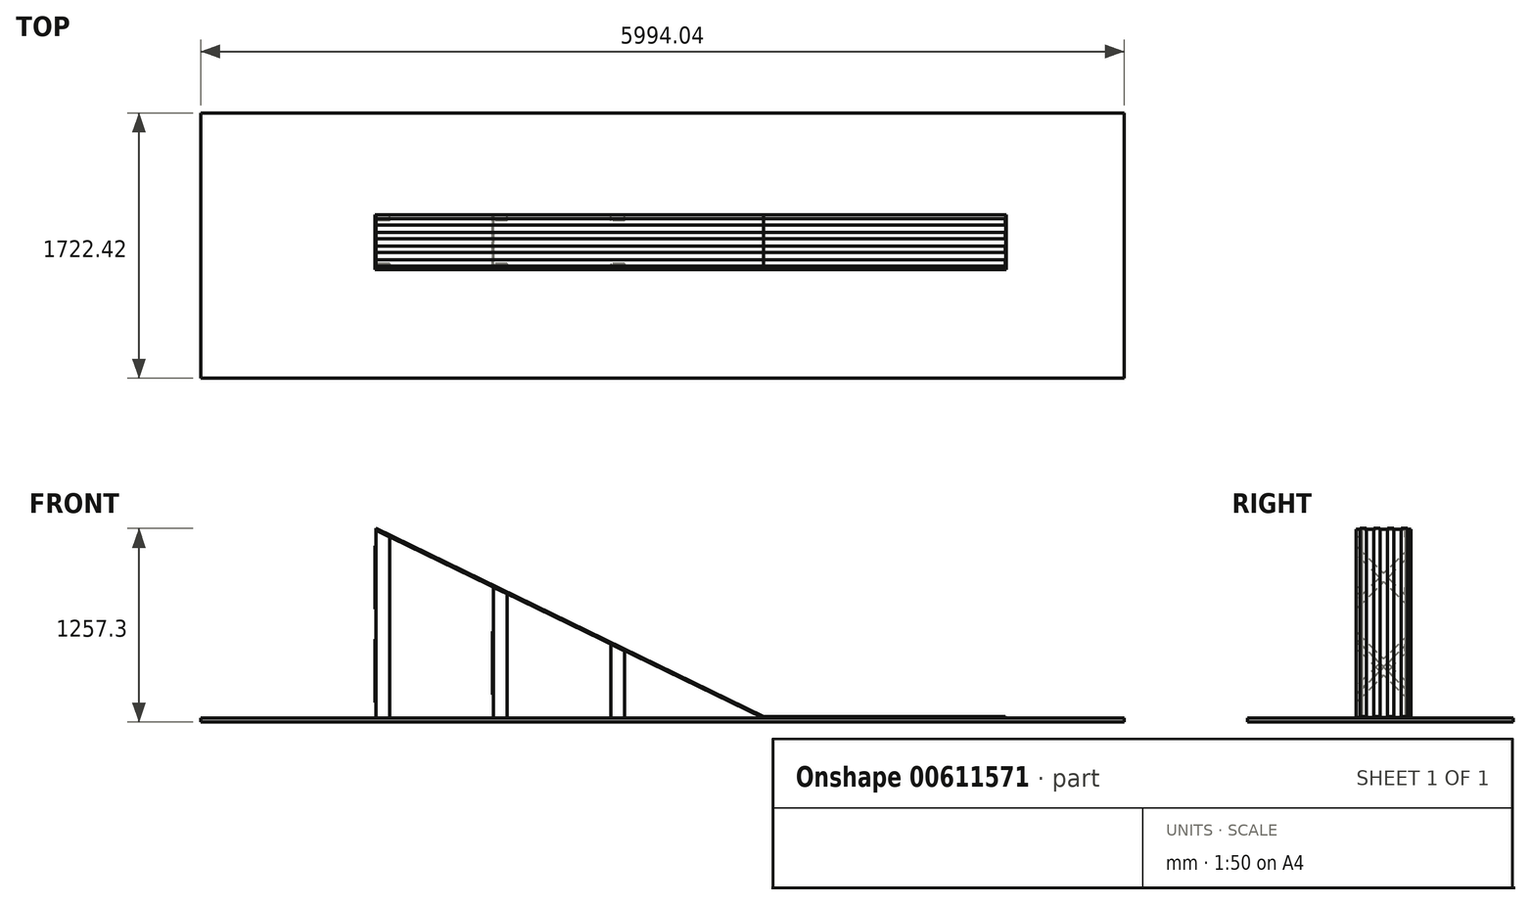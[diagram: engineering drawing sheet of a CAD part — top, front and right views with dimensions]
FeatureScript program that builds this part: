
annotation { "Feature Type Name" : "Feature", "Feature Type Description" : "" }
export const myFeature = defineFeature(function(context is Context, id is Id, definition is map)
    precondition{}
    {
        {
            var Q0;
            Q0=qCreatedBy(makeId("Front.planeOp"),FACE);
            var sketch = newSketch(context, id + "F0", { "sketchPlane" : qUnion([Q0])});
            skLineSegment(sketch, "E0", {"start": v(0, 0) * mm, "end": v(2514.6, -1219.2) * mm});
            skLineSegment(sketch, "E1", {"start": v(2514.6, -1219.2) * mm, "end": v(4089.4, -1219.2) * mm});
            skSolve(sketch);
        }
        {
            var Q0;
            Q0=qCreatedBy(makeId("Right.planeOp"),FACE);
            var sketch = newSketch(context, id + "F1", { "sketchPlane" : qUnion([Q0])});
            skLineSegment(sketch, "E2.bottom", {"start": v(177.8, 0) * mm, "end": v(-177.8, 0) * mm});
            skLineSegment(sketch, "E2.top", {"start": v(177.8, 6.35) * mm, "end": v(153.99, 6.35) * mm});
            skLineSegment(sketch, "E2.left", {"start": v(177.8, 0) * mm, "end": v(177.8, 6.35) * mm});
            skLineSegment(sketch, "E2.right", {"start": v(-177.8, 0) * mm, "end": v(-177.8, 6.35) * mm});
            skLineSegment(sketch, "E3.bottom", {"start": v(-153.99, 12.7) * mm, "end": v(-112.71, 12.7) * mm});
            skLineSegment(sketch, "E3.left", {"start": v(-153.99, 12.7) * mm, "end": v(-153.99, 6.35) * mm});
            skLineSegment(sketch, "E3.right", {"start": v(-112.71, 12.7) * mm, "end": v(-112.71, 6.35) * mm});
            skLineSegment(sketch, "E4.trimOffspring", {"start": v(-153.99, 6.35) * mm, "end": v(-177.8, 6.35) * mm});
            skLineSegment(sketch, "E5.bottom", {"start": v(-65.09, 12.7) * mm, "end": v(-23.81, 12.7) * mm});
            skLineSegment(sketch, "E5.left", {"start": v(-65.09, 12.7) * mm, "end": v(-65.09, 6.35) * mm});
            skLineSegment(sketch, "E5.right", {"start": v(-23.81, 12.7) * mm, "end": v(-23.81, 6.35) * mm});
            skLineSegment(sketch, "E6.trimOffspring", {"start": v(-65.09, 6.35) * mm, "end": v(-112.71, 6.35) * mm});
            skLineSegment(sketch, "E7.MirrorCS", {"start": v(153.99, 12.7) * mm, "end": v(153.99, 6.35) * mm});
            skLineSegment(sketch, "E8.MirrorCS", {"start": v(153.99, 12.7) * mm, "end": v(112.71, 12.7) * mm});
            skLineSegment(sketch, "E9.MirrorCS", {"start": v(65.09, 6.35) * mm, "end": v(112.71, 6.35) * mm});
            skLineSegment(sketch, "E10.MirrorCS", {"start": v(112.71, 12.7) * mm, "end": v(112.71, 6.35) * mm});
            skLineSegment(sketch, "E11.MirrorCS", {"start": v(153.99, 6.35) * mm, "end": v(177.8, 6.35) * mm});
            skLineSegment(sketch, "E12.MirrorCS", {"start": v(23.81, 12.7) * mm, "end": v(23.81, 6.35) * mm});
            skLineSegment(sketch, "E13.MirrorCS", {"start": v(65.09, 12.7) * mm, "end": v(23.81, 12.7) * mm});
            skLineSegment(sketch, "E14.MirrorCS", {"start": v(65.09, 12.7) * mm, "end": v(65.09, 6.35) * mm});
            skLineSegment(sketch, "E15.trimOffspring", {"start": v(23.81, 6.35) * mm, "end": v(-23.81, 6.35) * mm});
            skLineSegment(sketch, "E16.trimOffspring", {"start": v(112.71, 6.35) * mm, "end": v(65.09, 6.35) * mm});
            skSolve(sketch);
        }
        {
            var Q0;
            Q0=makeQuery(id+"F1.imprint","IMPRINT",FACE,{"disambiguationData":[TD([[makeQuery(id+"F1.imprint","IMPRINT",EDGE,{"derivedFrom":sQuery(id+"F1.wireOp",EDGE,"E2.bottom")}),-1.0]])]});
            var Q1;
            Q1=qConstructionFilter(qBodyType(qCreatedBy(id+"F0",EDGE),BodyType.WIRE),ConstructionObject.NO);
            sweep(context, id + "F2", {"profiles" : qUnion([Q0]), "path" : qUnion([Q1])});
        }
        {
            var Q0;
            Q0=qCreatedBy(makeId("Top.planeOp"),FACE);
            cPlane(context, id + "F3", {"entities" : qUnion([Q0]), "cplaneType" : CPlaneType.OFFSET, "offset" : 1219.2 * mm, "oppositeDirection" : true, "width" : 152.4 * mm, "height" : 152.4 * mm});
        }
        {
            var Q0;
            Q0=qCreatedBy(id+"F3.planeOp",FACE);
            var sketch = newSketch(context, id + "F4", { "sketchPlane" : qUnion([Q0])});
            skLineSegment(sketch, "E17.bottom", {"start": v(-1136.8, 840.01) * mm, "end": v(4857.24, 840.01) * mm});
            skLineSegment(sketch, "E17.top", {"start": v(-1136.8, -882.41) * mm, "end": v(4857.24, -882.41) * mm});
            skLineSegment(sketch, "E17.left", {"start": v(-1136.8, 840.01) * mm, "end": v(-1136.8, -882.41) * mm});
            skLineSegment(sketch, "E17.right", {"start": v(4857.24, 840.01) * mm, "end": v(4857.24, -882.41) * mm});
            skSolve(sketch);
        }
        {
            var Q0;
            Q0=makeQuery(id+"F4.imprint","IMPRINT",FACE,{"disambiguationData":[TD([[makeQuery(id+"F4.imprint","IMPRINT",EDGE,{"derivedFrom":sQuery(id+"F4.wireOp",EDGE,"E17.bottom")}),-1.0]])]});
            var Q1;
            Q1=sQuery(id+"F4.wireOp",EDGE,"E17.top");
            extrude(context, id + "F5", {"entities" : qUnion([Q0]), "surfaceEntities" : qUnion([Q1]), "oppositeDirection" : true, "depth" : 25.4 * mm, "offsetDistance" : 25.4 * mm});
        }
        {
            var Q0;
            Q0=qCreatedBy(id+"F3.planeOp",FACE);
            var sketch = newSketch(context, id + "F6", { "sketchPlane" : qUnion([Q0])});
            skLineSegment(sketch, "E18.bottom", {"start": v(0, 177.8) * mm, "end": v(88.9, 177.8) * mm});
            skLineSegment(sketch, "E18.top", {"start": v(0, 139.7) * mm, "end": v(88.9, 139.7) * mm});
            skLineSegment(sketch, "E18.left", {"start": v(0, 177.8) * mm, "end": v(0, 139.7) * mm});
            skLineSegment(sketch, "E18.right", {"start": v(88.9, 177.8) * mm, "end": v(88.9, 139.7) * mm});
            skLineSegment(sketch, "E19.bottom", {"start": v(762, 177.8) * mm, "end": v(850.9, 177.8) * mm});
            skLineSegment(sketch, "E19.top", {"start": v(762, 139.7) * mm, "end": v(850.9, 139.7) * mm});
            skLineSegment(sketch, "E19.left", {"start": v(762, 177.8) * mm, "end": v(762, 139.7) * mm});
            skLineSegment(sketch, "E19.right", {"start": v(850.9, 177.8) * mm, "end": v(850.9, 139.7) * mm});
            skLineSegment(sketch, "E20.bottom", {"start": v(1524, 177.8) * mm, "end": v(1612.9, 177.8) * mm});
            skLineSegment(sketch, "E20.top", {"start": v(1524, 139.7) * mm, "end": v(1612.9, 139.7) * mm});
            skLineSegment(sketch, "E20.left", {"start": v(1524, 177.8) * mm, "end": v(1524, 139.7) * mm});
            skLineSegment(sketch, "E20.right", {"start": v(1612.9, 177.8) * mm, "end": v(1612.9, 139.7) * mm});
            skLineSegment(sketch, "E21.MirrorCS", {"start": v(88.9, -177.8) * mm, "end": v(88.9, -139.7) * mm});
            skLineSegment(sketch, "E22.MirrorCS", {"start": v(0, -139.7) * mm, "end": v(88.9, -139.7) * mm});
            skLineSegment(sketch, "E23.MirrorCS", {"start": v(0, -177.8) * mm, "end": v(0, -139.7) * mm});
            skLineSegment(sketch, "E24.MirrorCS", {"start": v(762, -177.8) * mm, "end": v(850.9, -177.8) * mm});
            skLineSegment(sketch, "E25.MirrorCS", {"start": v(762, -139.7) * mm, "end": v(850.9, -139.7) * mm});
            skLineSegment(sketch, "E26.MirrorCS", {"start": v(0, -177.8) * mm, "end": v(88.9, -177.8) * mm});
            skLineSegment(sketch, "E27.MirrorCS", {"start": v(1612.9, -177.8) * mm, "end": v(1612.9, -139.7) * mm});
            skLineSegment(sketch, "E28.MirrorCS", {"start": v(1524, -177.8) * mm, "end": v(1524, -139.7) * mm});
            skLineSegment(sketch, "E29.MirrorCS", {"start": v(1524, -139.7) * mm, "end": v(1612.9, -139.7) * mm});
            skLineSegment(sketch, "E30.MirrorCS", {"start": v(762, -177.8) * mm, "end": v(762, -139.7) * mm});
            skLineSegment(sketch, "E31.MirrorCS", {"start": v(1524, -177.8) * mm, "end": v(1612.9, -177.8) * mm});
            skLineSegment(sketch, "E32.MirrorCS", {"start": v(850.9, -177.8) * mm, "end": v(850.9, -139.7) * mm});
            skSolve(sketch);
        }
        {
            var Q0;
            Q0=qSketchRegion(id+"F6",true);
            var Q1;
            Q1=makeQuery(id+"F2.opSweep","SWEPT_FACE",FACE,{"disambiguationData":[OSD([sQuery(id+"F0.wireOp",EDGE,"E0"),sQuery(id+"F1.wireOp",EDGE,"E2.bottom")])]});
            extrude(context, id + "F7", {"entities" : qUnion([Q0]), "endBound" : BoundingType.UP_TO_SURFACE, "depth" : 25.4 * mm, "endBoundEntityFace" : qUnion([Q1]), "offsetDistance" : 25.4 * mm});
        }
        {
            var Q0;
            Q0=qCreatedBy(makeId("Right.planeOp"),FACE);
            var sketch = newSketch(context, id + "F8", { "sketchPlane" : qUnion([Q0])});
            skLineSegment(sketch, "E33", {"start": v(177.8, -101.6) * mm, "end": v(0, -279.4) * mm});
            skLineSegment(sketch, "E34", {"start": v(-177.8, -511.08) * mm, "end": v(-177.8, -457.2) * mm});
            skLineSegment(sketch, "E35", {"start": v(-177.8, -511.08) * mm, "end": v(0, -333.28) * mm});
            skLineSegment(sketch, "E36", {"start": v(177.8, -101.6) * mm, "end": v(177.8, -155.48) * mm});
            skLineSegment(sketch, "E37", {"start": v(-177.8, -511.08) * mm, "end": v(-204.74, -484.14) * mm, "construction": true});
            skLineSegment(sketch, "E38", {"start": v(-204.74, -484.14) * mm, "end": v(-177.8, -457.2) * mm, "construction": true});
            skLineSegment(sketch, "E39", {"start": v(177.8, -155.48) * mm, "end": v(204.74, -128.54) * mm, "construction": true});
            skLineSegment(sketch, "E40", {"start": v(204.74, -128.54) * mm, "end": v(177.8, -101.6) * mm, "construction": true});
            skLineSegment(sketch, "E41", {"start": v(130.23, -609.6) * mm, "end": v(-102.74, -609.6) * mm, "construction": true});
            skLineSegment(sketch, "E42.MirrorCS", {"start": v(177.8, -511.08) * mm, "end": v(177.8, -457.2) * mm});
            skLineSegment(sketch, "E43.MirrorCS", {"start": v(-177.8, -101.6) * mm, "end": v(-177.8, -155.48) * mm});
            skLineSegment(sketch, "E44.MirrorCS", {"start": v(177.8, -511.08) * mm, "end": v(0, -333.28) * mm});
            skLineSegment(sketch, "E45.MirrorCS", {"start": v(-177.8, -101.6) * mm, "end": v(0, -279.4) * mm});
            skLineSegment(sketch, "E46.trimOffspring", {"start": v(26.94, -306.34) * mm, "end": v(177.8, -155.48) * mm});
            skLineSegment(sketch, "E47.trimOffspring", {"start": v(26.94, -306.34) * mm, "end": v(177.8, -457.2) * mm});
            skLineSegment(sketch, "E48.trimOffspring", {"start": v(-26.94, -306.34) * mm, "end": v(-177.8, -457.2) * mm});
            skLineSegment(sketch, "E49.trimOffspring", {"start": v(-26.94, -306.34) * mm, "end": v(-177.8, -155.48) * mm});
            skLineSegment(sketch, "E50.MirrorCS", {"start": v(-204.74, -735.06) * mm, "end": v(-177.8, -762) * mm, "construction": true});
            skLineSegment(sketch, "E51.MirrorCS", {"start": v(177.8, -1063.72) * mm, "end": v(204.74, -1090.66) * mm, "construction": true});
            skLineSegment(sketch, "E52.MirrorCS", {"start": v(-177.8, -708.12) * mm, "end": v(-204.74, -735.06) * mm, "construction": true});
            skLineSegment(sketch, "E53.MirrorCS", {"start": v(204.74, -1090.66) * mm, "end": v(177.8, -1117.6) * mm, "construction": true});
            skLineSegment(sketch, "E54.MirrorCS", {"start": v(26.94, -912.86) * mm, "end": v(177.8, -1063.72) * mm});
            skLineSegment(sketch, "E55.MirrorCS", {"start": v(26.94, -912.86) * mm, "end": v(177.8, -762) * mm});
            skLineSegment(sketch, "E56.MirrorCS", {"start": v(-26.94, -912.86) * mm, "end": v(-177.8, -762) * mm});
            skLineSegment(sketch, "E57.MirrorCS", {"start": v(177.8, -1117.6) * mm, "end": v(0, -939.8) * mm});
            skLineSegment(sketch, "E58.MirrorCS", {"start": v(-177.8, -708.12) * mm, "end": v(0, -885.92) * mm});
            skLineSegment(sketch, "E59.MirrorCS", {"start": v(177.8, -708.12) * mm, "end": v(177.8, -762) * mm});
            skLineSegment(sketch, "E60.MirrorCS", {"start": v(-26.94, -912.86) * mm, "end": v(-177.8, -1063.72) * mm});
            skLineSegment(sketch, "E61.MirrorCS", {"start": v(-177.8, -1117.6) * mm, "end": v(-177.8, -1063.72) * mm});
            skLineSegment(sketch, "E62.MirrorCS", {"start": v(-177.8, -708.12) * mm, "end": v(-177.8, -762) * mm});
            skLineSegment(sketch, "E63.MirrorCS", {"start": v(177.8, -1117.6) * mm, "end": v(177.8, -1063.72) * mm});
            skLineSegment(sketch, "E64.MirrorCS", {"start": v(177.8, -708.12) * mm, "end": v(0, -885.92) * mm});
            skLineSegment(sketch, "E65.MirrorCS", {"start": v(-177.8, -1117.6) * mm, "end": v(0, -939.8) * mm});
            skSolve(sketch);
        }
        {
            var Q0;
            Q0=qSketchRegion(id+"F8",true);
            extrude(context, id + "F9", {"entities" : qUnion([Q0]), "oppositeDirection" : true, "depth" : 6.35 * mm, "offsetDistance" : 25.4 * mm});
        }
        {
            var Q0;
            Q0=makeQuery(id+"F7.opExtrude","SWEPT_FACE",FACE,{"disambiguationData":[OSD([sQuery(id+"F6.wireOp",EDGE,"E19.left")])]});
            var sketch = newSketch(context, id + "F10", { "sketchPlane" : qUnion([Q0])});
            skLineSegment(sketch, "E66", {"start": v(177.8, -657.32) * mm, "end": v(0, -835.12) * mm});
            skLineSegment(sketch, "E67", {"start": v(-177.8, -1066.8) * mm, "end": v(-177.8, -1012.92) * mm});
            skLineSegment(sketch, "E68", {"start": v(-177.8, -1066.8) * mm, "end": v(0, -889) * mm});
            skLineSegment(sketch, "E69", {"start": v(177.8, -657.32) * mm, "end": v(177.8, -711.2) * mm});
            skLineSegment(sketch, "E70", {"start": v(-177.8, -1066.8) * mm, "end": v(-204.74, -1039.86) * mm, "construction": true});
            skLineSegment(sketch, "E71", {"start": v(-204.74, -1039.86) * mm, "end": v(-177.8, -1012.92) * mm, "construction": true});
            skLineSegment(sketch, "E72", {"start": v(177.8, -711.2) * mm, "end": v(204.74, -684.26) * mm, "construction": true});
            skLineSegment(sketch, "E73", {"start": v(204.74, -684.26) * mm, "end": v(177.8, -657.32) * mm, "construction": true});
            skLineSegment(sketch, "E74.MirrorCS", {"start": v(177.8, -1066.8) * mm, "end": v(177.8, -1012.92) * mm});
            skLineSegment(sketch, "E75.MirrorCS", {"start": v(-177.8, -657.32) * mm, "end": v(-177.8, -711.2) * mm});
            skLineSegment(sketch, "E76.MirrorCS", {"start": v(177.8, -1066.8) * mm, "end": v(0, -889) * mm});
            skLineSegment(sketch, "E77.MirrorCS", {"start": v(-177.8, -657.32) * mm, "end": v(0, -835.12) * mm});
            skLineSegment(sketch, "E78.trimOffspring", {"start": v(26.94, -862.06) * mm, "end": v(177.8, -711.2) * mm});
            skLineSegment(sketch, "E79.trimOffspring", {"start": v(26.94, -862.06) * mm, "end": v(177.8, -1012.92) * mm});
            skLineSegment(sketch, "E80.trimOffspring", {"start": v(-26.94, -862.06) * mm, "end": v(-177.8, -1012.92) * mm});
            skLineSegment(sketch, "E81.trimOffspring", {"start": v(-26.94, -862.06) * mm, "end": v(-177.8, -711.2) * mm});
            skSolve(sketch);
        }
        {
            var Q0;
            Q0=qSketchRegion(id+"F10",true);
            extrude(context, id + "F11", {"entities" : qUnion([Q0]), "depth" : 6.35 * mm, "offsetDistance" : 25.4 * mm});
        }
    });
